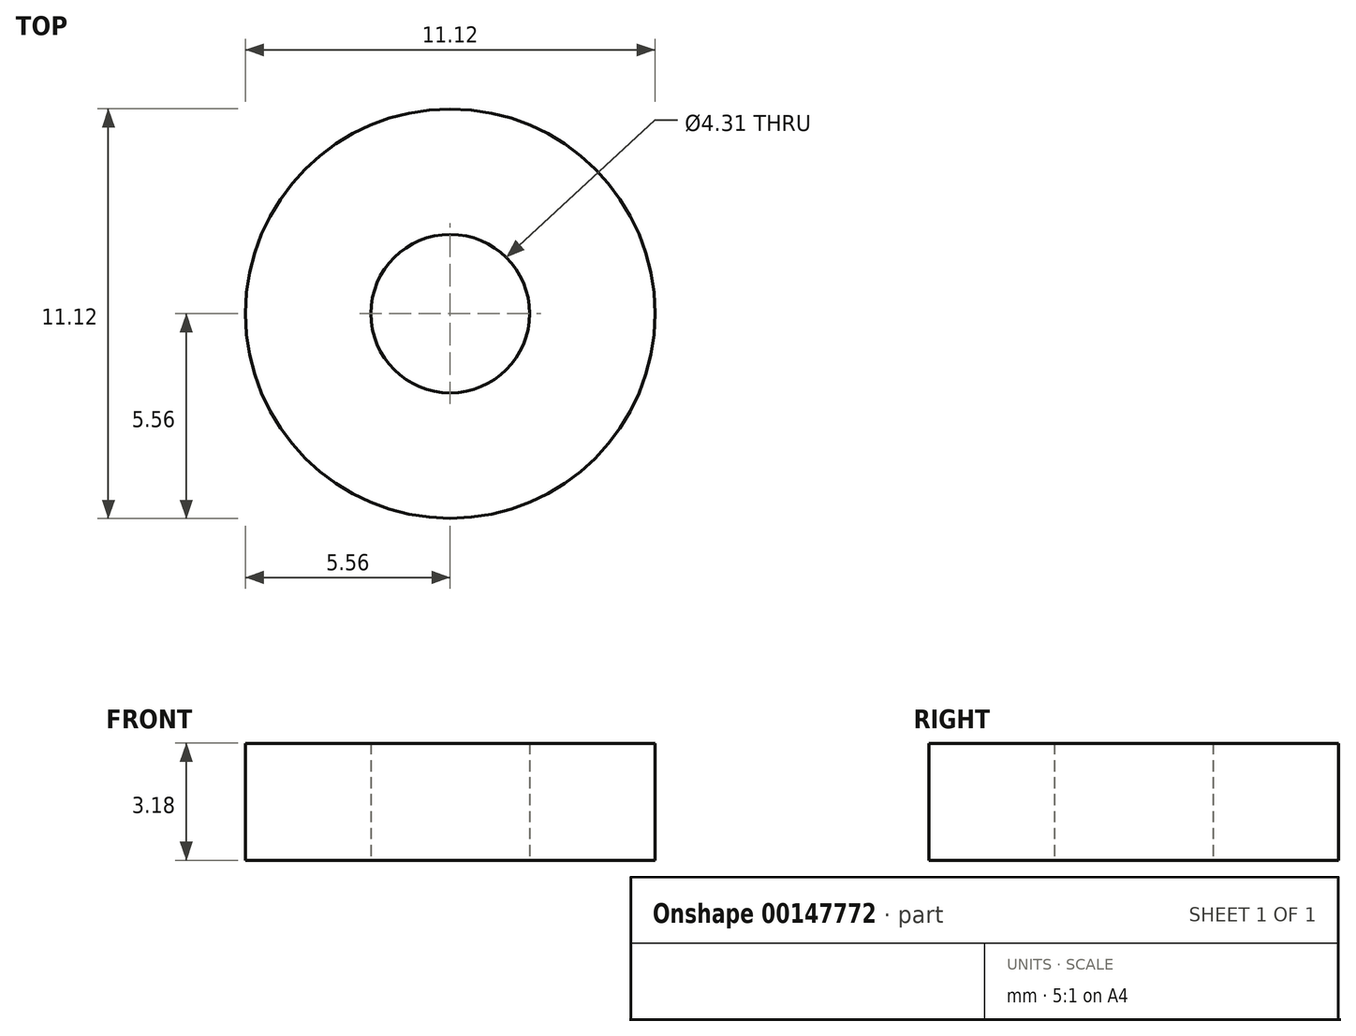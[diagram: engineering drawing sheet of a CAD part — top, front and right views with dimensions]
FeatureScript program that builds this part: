
annotation { "Feature Type Name" : "Feature", "Feature Type Description" : "" }
export const myFeature = defineFeature(function(context is Context, id is Id, definition is map)
    precondition{}
    {
        {
            var Q0;
            Q0=qCreatedBy(makeId("Top.planeOp"),FACE);
            var sketch = newSketch(context, id + "F0", { "sketchPlane" : qUnion([Q0])});
            skCircle(sketch, "E0", {"center": v(0, 0) * mm, "radius": 5.56 * mm});
            skCircle(sketch, "E1", {"center": v(0, 0) * mm, "radius": 2.15 * mm});
            skSolve(sketch);
        }
        {
            var Q0;
            Q0=qSketchRegion(id+"F0",true);
            extrude(context, id + "F1", {"entities" : qUnion([Q0]), "depth" : 3.17 * mm});
        }
    });
